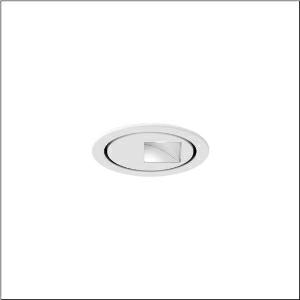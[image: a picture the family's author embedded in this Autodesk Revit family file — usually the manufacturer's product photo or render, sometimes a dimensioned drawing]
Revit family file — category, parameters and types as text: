
# Revit family: lunis_11_micro_round_51dj11cd1wm21
name_source: partatom
category: Lighting Fixtures
units: mm (PartAtom-declared; Revit-internal decimal feet)

## family parameters
Cut with Voids When Loaded = No
Host = Face
Light Source = No
Part Type = Normal
Room Calculation Point = No
Round Connector Dimension = Use Diameter
Shared = No

## types (1)
- Lunis 11 micro round (1 x LED 3000K / CRI = 90 (unbekannt), 1100 lm, 3000K)
    Apparent Load = 20 VA
    CIE Flux Codes = 42 75 96 100 100
    Color Rendering = 90
    Color Temperature = 3000K
    Default Elevation = 1800 mm
    Description = Lunis 11 micro round, downlight, light control with wallwasher, of highly reflective aluminium, highly specular, light emission: direct distribution, LED rated luminous flux: 1.100lm, light colour: 930, with terminal, 5-pole, mains connection: 220..230V, AC, 50/60Hz, LED module, of aluminium, highly specular, white, diameter: 114mm, clamping range: 1..40mm, recessing ring, of plastic, traffic white (RAL 9016), protection rating (complete): IP20, insulation class (complete): insulation class II (safety insulation), certification: CE, permissible ambient temperature for indoor applications: 0..+35°C, packaging unit: 1 piece
    Height = 0 mm  [stored 0 ft]
    Lamp = 1 x LED 3000K / CRI >= 90 (unbekannt)
    Lamp Light Flux = 1100 lm
    Lamp count = 1
    Length = 114 mm
    Luminous efficacy = 56 lm/W
    Manufacturer = Siteco
    ModVariant = No
    Model = 51DJ11CD1WM21
    Mounting Place = Ceiling
    Mounting Type = Recessed
    Number of Poles = 1
    OnlyDefault = Yes
    Power Factor = 1
    Product Name = Lunis 11 micro round
    Product group = downlight
    ProductGroupID = 400
    Protection Class = Protection class II
    Protection Degree = IP 20
    RLX_Detail_Level = 1
    RLX_Emergency_Light_Flux = 0 lm
    RLX_Emergency_Type = 0
    RLX_Emergency_Type_DB = No
    RlxData = <blob elided: 40789 chars, md5=967c0bae>
    Socket = socket
    Standby Power = 0 W
    System Light Flux = 1100 lm
    System Power = 20 W
    Type Comments = Product without accessories
    Type Image = l_1004773.jpg
    URL = http://relux.com
    VarID = ---
    Voltage = 0 V
    Weight = 0.00 kg
    Width = 114 mm

note: [stored X ft] marks values corroborated as IEEE doubles in the binary element streams (Revit-internal decimal feet)

## geometry (parser evidence)
native form markers: Blend x4, Sweep x11
no freeform markers — native parametric forms only
